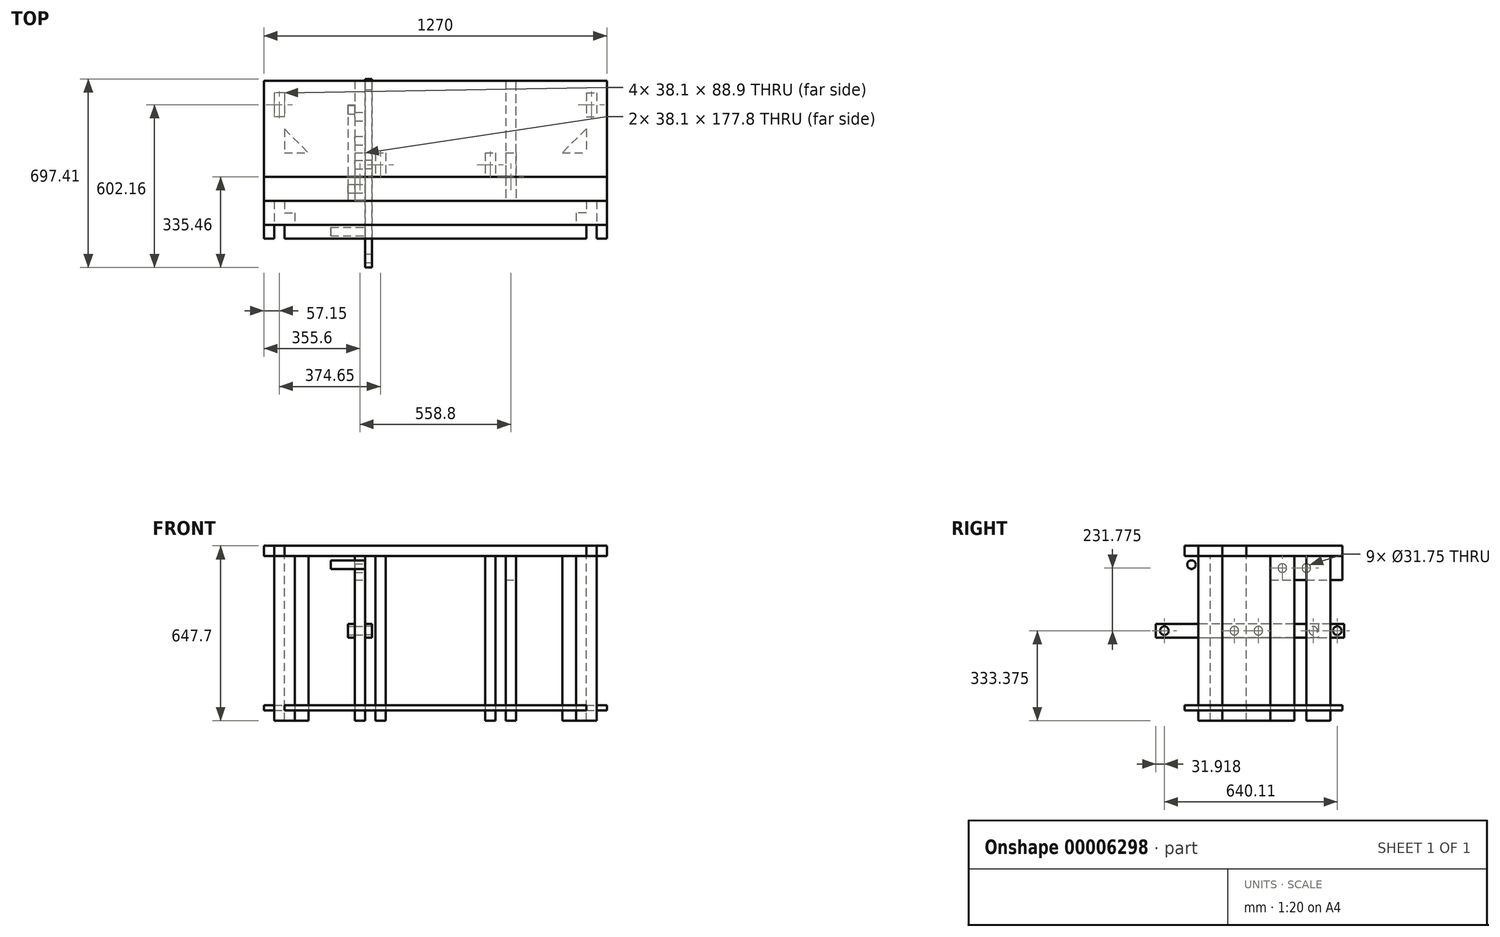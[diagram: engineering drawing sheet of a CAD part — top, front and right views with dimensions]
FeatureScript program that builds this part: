
annotation { "Feature Type Name" : "Feature", "Feature Type Description" : "" }
export const myFeature = defineFeature(function(context is Context, id is Id, definition is map)
    precondition{}
    {
        {
            var Q0;
            Q0=qCreatedBy(makeId("Top.planeOp"),FACE);
            var sketch = newSketch(context, id + "F0", { "sketchPlane" : qUnion([Q0])});
            skLineSegment(sketch, "E0.rect.bottom", {"start": v(635, -292.1) * mm, "end": v(-635, -292.1) * mm});
            skLineSegment(sketch, "E0.rect.top", {"start": v(635, 292.1) * mm, "end": v(558.8, 292.1) * mm});
            skLineSegment(sketch, "E0.rect.left", {"start": v(635, -292.1) * mm, "end": v(635, 292.1) * mm});
            skLineSegment(sketch, "E0.rect.right", {"start": v(-635, -292.1) * mm, "end": v(-635, 292.1) * mm});
            skPoint(sketch, "E0.rect.middle", {"position": v(0, 0) * mm});
            skLineSegment(sketch, "E1", {"start": v(-558.8, 292.1) * mm, "end": v(-558.8, 203.2) * mm});
            skLineSegment(sketch, "E2", {"start": v(-558.8, 203.2) * mm, "end": v(-558.8, 114.3) * mm});
            skLineSegment(sketch, "E3", {"start": v(-558.8, 114.3) * mm, "end": v(-558.8, 25.4) * mm});
            skLineSegment(sketch, "E4", {"start": v(-558.8, 203.2) * mm, "end": v(558.8, 203.2) * mm});
            skLineSegment(sketch, "E5", {"start": v(-558.8, 114.3) * mm, "end": v(558.8, 114.3) * mm});
            skLineSegment(sketch, "E6", {"start": v(-558.8, 25.4) * mm, "end": v(558.8, 25.4) * mm});
            skLineSegment(sketch, "E7", {"start": v(-558.8, 114.3) * mm, "end": v(-469.9, 25.4) * mm});
            skLineSegment(sketch, "E8", {"start": v(558.8, 114.3) * mm, "end": v(469.9, 25.4) * mm});
            skLineSegment(sketch, "E9", {"start": v(-298.45, 292.1) * mm, "end": v(-298.45, 25.4) * mm});
            skLineSegment(sketch, "E10", {"start": v(298.45, 25.4) * mm, "end": v(298.45, 292.1) * mm});
            skLineSegment(sketch, "E11", {"start": v(558.8, 292.1) * mm, "end": v(558.8, 25.4) * mm});
            skLineSegment(sketch, "E12", {"start": v(-558.8, 25.4) * mm, "end": v(-558.8, -63.5) * mm, "construction": true});
            skLineSegment(sketch, "E13", {"start": v(-558.8, -63.5) * mm, "end": v(-558.8, -152.4) * mm, "construction": true});
            skLineSegment(sketch, "E14", {"start": v(-558.8, -152.4) * mm, "end": v(-558.8, -241.3) * mm, "construction": true});
            skLineSegment(sketch, "E15", {"start": v(-558.8, -63.5) * mm, "end": v(558.8, -63.5) * mm, "construction": true});
            skLineSegment(sketch, "E16", {"start": v(-558.8, -152.4) * mm, "end": v(558.8, -152.4) * mm, "construction": true});
            skLineSegment(sketch, "E17", {"start": v(-558.8, -241.3) * mm, "end": v(558.8, -241.3) * mm, "construction": true});
            skLineSegment(sketch, "E18", {"start": v(558.8, 25.4) * mm, "end": v(558.8, -241.3) * mm, "construction": true});
            skLineSegment(sketch, "E19", {"start": v(-558.8, 292.1) * mm, "end": v(-635, 292.1) * mm});
            skLineSegment(sketch, "E20", {"start": v(-298.45, 292.1) * mm, "end": v(-558.8, 292.1) * mm});
            skLineSegment(sketch, "E21", {"start": v(298.45, 292.1) * mm, "end": v(298.45, 292.1) * mm});
            skLineSegment(sketch, "E22", {"start": v(558.8, 292.1) * mm, "end": v(298.45, 292.1) * mm});
            skLineSegment(sketch, "E23", {"start": v(-298.45, 292.1) * mm, "end": v(298.45, 292.1) * mm});
            skLineSegment(sketch, "E24", {"start": v(-260.35, 292.1) * mm, "end": v(-260.35, 25.4) * mm});
            skLineSegment(sketch, "E25", {"start": v(260.35, 292.1) * mm, "end": v(260.35, 25.4) * mm});
            skLineSegment(sketch, "E26", {"start": v(-298.45, 25.4) * mm, "end": v(-298.45, -241.3) * mm});
            skLineSegment(sketch, "E27", {"start": v(-260.35, 25.4) * mm, "end": v(-260.35, -241.3) * mm});
            skLineSegment(sketch, "E28", {"start": v(-222.25, 25.4) * mm, "end": v(-222.25, -63.5) * mm});
            skLineSegment(sketch, "E29", {"start": v(-184.15, 25.4) * mm, "end": v(-184.15, -63.5) * mm});
            skLineSegment(sketch, "E30.bottom", {"start": v(-558.8, -152.4) * mm, "end": v(-520.7, -152.4) * mm});
            skLineSegment(sketch, "E30.top", {"start": v(-558.8, -241.3) * mm, "end": v(-520.7, -241.3) * mm});
            skLineSegment(sketch, "E30.left", {"start": v(-558.8, -152.4) * mm, "end": v(-558.8, -241.3) * mm});
            skLineSegment(sketch, "E30.right", {"start": v(-520.7, -152.4) * mm, "end": v(-520.7, -241.3) * mm});
            skLineSegment(sketch, "E31.bottom", {"start": v(558.8, -152.4) * mm, "end": v(520.7, -152.4) * mm});
            skLineSegment(sketch, "E31.top", {"start": v(558.8, -241.3) * mm, "end": v(520.7, -241.3) * mm});
            skLineSegment(sketch, "E31.left", {"start": v(558.8, -152.4) * mm, "end": v(558.8, -241.3) * mm});
            skLineSegment(sketch, "E31.right", {"start": v(520.7, -152.4) * mm, "end": v(520.7, -241.3) * mm});
            skLineSegment(sketch, "E32", {"start": v(260.35, 25.4) * mm, "end": v(260.35, -241.3) * mm});
            skLineSegment(sketch, "E33", {"start": v(298.45, 25.4) * mm, "end": v(298.45, -241.3) * mm});
            skLineSegment(sketch, "E34", {"start": v(222.25, 25.4) * mm, "end": v(222.25, -63.5) * mm});
            skLineSegment(sketch, "E35", {"start": v(184.15, 25.4) * mm, "end": v(184.15, -63.5) * mm});
            skLineSegment(sketch, "E36", {"start": v(-222.25, -63.5) * mm, "end": v(-184.15, -63.5) * mm});
            skLineSegment(sketch, "E37", {"start": v(184.15, -63.5) * mm, "end": v(222.25, -63.5) * mm});
            skLineSegment(sketch, "E38", {"start": v(-298.45, -241.3) * mm, "end": v(-260.35, -241.3) * mm});
            skLineSegment(sketch, "E39", {"start": v(260.35, -241.3) * mm, "end": v(298.45, -241.3) * mm});
            skLineSegment(sketch, "E40", {"start": v(-298.45, -152.4) * mm, "end": v(-260.35, -152.4) * mm});
            skLineSegment(sketch, "E41", {"start": v(260.35, -152.4) * mm, "end": v(298.45, -152.4) * mm});
            skLineSegment(sketch, "E42", {"start": v(-558.8, 247.65) * mm, "end": v(-596.9, 247.65) * mm});
            skLineSegment(sketch, "E43", {"start": v(-596.9, 247.65) * mm, "end": v(-596.9, -292.1) * mm});
            skLineSegment(sketch, "E44", {"start": v(-596.9, -292.1) * mm, "end": v(-558.8, -292.1) * mm});
            skLineSegment(sketch, "E45", {"start": v(-558.8, -292.1) * mm, "end": v(-558.8, -241.3) * mm});
            skLineSegment(sketch, "E46", {"start": v(558.8, 247.65) * mm, "end": v(596.9, 247.65) * mm});
            skLineSegment(sketch, "E47", {"start": v(596.9, 247.65) * mm, "end": v(596.9, -292.1) * mm});
            skLineSegment(sketch, "E48", {"start": v(596.9, -292.1) * mm, "end": v(558.8, -292.1) * mm});
            skLineSegment(sketch, "E49", {"start": v(558.8, -292.1) * mm, "end": v(558.8, -241.3) * mm});
            skLineSegment(sketch, "E50", {"start": v(-558.8, 25.4) * mm, "end": v(-635, 25.4) * mm});
            skLineSegment(sketch, "E51", {"start": v(558.8, 25.4) * mm, "end": v(635, 25.4) * mm});
            skLineSegment(sketch, "E52", {"start": v(-635, -63.5) * mm, "end": v(635, -63.5) * mm});
            skLineSegment(sketch, "E53", {"start": v(-635, -152.4) * mm, "end": v(635, -152.4) * mm});
            skLineSegment(sketch, "E54", {"start": v(-635, -241.3) * mm, "end": v(635, -241.3) * mm});
            skLineSegment(sketch, "E55", {"start": v(558.8, 158.75) * mm, "end": v(596.9, 158.75) * mm});
            skLineSegment(sketch, "E56", {"start": v(-558.8, 158.75) * mm, "end": v(-596.9, 158.75) * mm});
            skLineSegment(sketch, "E57", {"start": v(-558.8, -196.85) * mm, "end": v(-520.7, -196.85) * mm});
            skLineSegment(sketch, "E58", {"start": v(558.8, -196.85) * mm, "end": v(520.7, -196.85) * mm});
            skLineSegment(sketch, "E59", {"start": v(-520.7, -241.3) * mm, "end": v(-520.7, -292.1) * mm});
            skLineSegment(sketch, "E60", {"start": v(520.7, -241.3) * mm, "end": v(520.7, -292.1) * mm});
            skSolve(sketch);
        }
        {
            var Q0;
            {var subQ3=sQuery(id+"F0.wireOp",EDGE,"E0.rect.right");var subQ5=sQuery(id+"F0.wireOp",EDGE,"E50");var subQ7=makeQuery(id+"F0.imprint","INTERSECT",VERTEX,{"derivedFrom":[subQ3,subQ5]});Q0=makeQuery(id+"F0.imprint","IMPRINT",FACE,{"disambiguationData":[TD([[makeQuery(id+"F0.imprint","IMPRINT",EDGE,{"disambiguationData":[TD([[subQ7,1.0]])],"derivedFrom":subQ3}),-1.0]])]});}
            var Q1;
            {var subQ1=sQuery(id+"F0.wireOp",EDGE,"E43");var subQ5=sQuery(id+"F0.wireOp",EDGE,"E50");var subQ6=makeQuery(id+"F0.imprint","INTERSECT",VERTEX,{"derivedFrom":[subQ1,subQ5]});Q1=makeQuery(id+"F0.imprint","IMPRINT",FACE,{"disambiguationData":[TD([[makeQuery(id+"F0.imprint","IMPRINT",EDGE,{"disambiguationData":[TD([[subQ6,-1.0]])],"derivedFrom":subQ1}),1.0]])]});}
            var Q2;
            {var subQ0=sQuery(id+"F0.wireOp",EDGE,"E52");var subQ3=sQuery(id+"F0.wireOp",EDGE,"E26");var subQ4=makeQuery(id+"F0.imprint","INTERSECT",VERTEX,{"derivedFrom":[subQ3,subQ0]});Q2=makeQuery(id+"F0.imprint","IMPRINT",FACE,{"disambiguationData":[TD([[makeQuery(id+"F0.imprint","IMPRINT",EDGE,{"disambiguationData":[TD([[subQ4,-1.0]])],"derivedFrom":subQ0}),1.0]])]});}
            var Q3;
            {var subQ3=sQuery(id+"F0.wireOp",EDGE,"E28");Q3=makeQuery(id+"F0.imprint","IMPRINT",FACE,{"disambiguationData":[TD([[makeQuery(id+"F0.imprint","IMPRINT",EDGE,{"derivedFrom":subQ3}),-1.0]])]});}
            var Q4;
            {var subQ2=sQuery(id+"F0.wireOp",EDGE,"E28");Q4=makeQuery(id+"F0.imprint","IMPRINT",FACE,{"disambiguationData":[TD([[makeQuery(id+"F0.imprint","IMPRINT",EDGE,{"derivedFrom":subQ2}),1.0]])]});}
            var Q5;
            {var subQ2=sQuery(id+"F0.wireOp",EDGE,"E29");Q5=makeQuery(id+"F0.imprint","IMPRINT",FACE,{"disambiguationData":[TD([[makeQuery(id+"F0.imprint","IMPRINT",EDGE,{"derivedFrom":subQ2}),1.0]])]});}
            var Q6;
            {var subQ2=sQuery(id+"F0.wireOp",EDGE,"E34");Q6=makeQuery(id+"F0.imprint","IMPRINT",FACE,{"disambiguationData":[TD([[makeQuery(id+"F0.imprint","IMPRINT",EDGE,{"derivedFrom":subQ2}),-1.0]])]});}
            var Q7;
            {var subQ3=sQuery(id+"F0.wireOp",EDGE,"E34");Q7=makeQuery(id+"F0.imprint","IMPRINT",FACE,{"disambiguationData":[TD([[makeQuery(id+"F0.imprint","IMPRINT",EDGE,{"derivedFrom":subQ3}),1.0]])]});}
            var Q8;
            {var subQ0=sQuery(id+"F0.wireOp",EDGE,"E52");var subQ3=sQuery(id+"F0.wireOp",EDGE,"E32");var subQ4=makeQuery(id+"F0.imprint","INTERSECT",VERTEX,{"derivedFrom":[subQ3,subQ0]});Q8=makeQuery(id+"F0.imprint","IMPRINT",FACE,{"disambiguationData":[TD([[makeQuery(id+"F0.imprint","IMPRINT",EDGE,{"disambiguationData":[TD([[subQ4,-1.0]])],"derivedFrom":subQ0}),1.0]])]});}
            var Q9;
            {var subQ1=sQuery(id+"F0.wireOp",EDGE,"E47");var subQ5=sQuery(id+"F0.wireOp",EDGE,"E51");var subQ6=makeQuery(id+"F0.imprint","INTERSECT",VERTEX,{"derivedFrom":[subQ1,subQ5]});Q9=makeQuery(id+"F0.imprint","IMPRINT",FACE,{"disambiguationData":[TD([[makeQuery(id+"F0.imprint","IMPRINT",EDGE,{"disambiguationData":[TD([[subQ6,-1.0]])],"derivedFrom":subQ1}),-1.0]])]});}
            var Q10;
            {var subQ3=sQuery(id+"F0.wireOp",EDGE,"E0.rect.left");var subQ5=sQuery(id+"F0.wireOp",EDGE,"E51");var subQ7=makeQuery(id+"F0.imprint","INTERSECT",VERTEX,{"derivedFrom":[subQ3,subQ5]});Q10=makeQuery(id+"F0.imprint","IMPRINT",FACE,{"disambiguationData":[TD([[makeQuery(id+"F0.imprint","IMPRINT",EDGE,{"disambiguationData":[TD([[subQ7,1.0]])],"derivedFrom":subQ3}),1.0]])]});}
            var Q11;
            {var subQ3=sQuery(id+"F0.wireOp",EDGE,"E0.rect.right");var subQ5=sQuery(id+"F0.wireOp",EDGE,"E53");var subQ7=makeQuery(id+"F0.imprint","INTERSECT",VERTEX,{"derivedFrom":[subQ3,subQ5]});Q11=makeQuery(id+"F0.imprint","IMPRINT",FACE,{"disambiguationData":[TD([[makeQuery(id+"F0.imprint","IMPRINT",EDGE,{"disambiguationData":[TD([[subQ7,1.0]])],"derivedFrom":subQ3}),-1.0]])]});}
            var Q12;
            {var subQ3=sQuery(id+"F0.wireOp",EDGE,"E30.left");Q12=makeQuery(id+"F0.imprint","IMPRINT",FACE,{"disambiguationData":[TD([[makeQuery(id+"F0.imprint","IMPRINT",EDGE,{"derivedFrom":subQ3}),-1.0]])]});}
            var Q13;
            {var subQ2=sQuery(id+"F0.wireOp",EDGE,"E30.left");Q13=makeQuery(id+"F0.imprint","IMPRINT",FACE,{"disambiguationData":[TD([[makeQuery(id+"F0.imprint","IMPRINT",EDGE,{"derivedFrom":subQ2}),1.0]])]});}
            var Q14;
            {var subQ1=sQuery(id+"F0.wireOp",EDGE,"E30.right");Q14=makeQuery(id+"F0.imprint","IMPRINT",FACE,{"disambiguationData":[TD([[makeQuery(id+"F0.imprint","IMPRINT",EDGE,{"derivedFrom":subQ1}),1.0]])]});}
            var Q15;
            {var subQ0=sQuery(id+"F0.wireOp",EDGE,"E54");var subQ3=sQuery(id+"F0.wireOp",EDGE,"E26");var subQ4=makeQuery(id+"F0.imprint","INTERSECT",VERTEX,{"derivedFrom":[subQ3,subQ0]});Q15=makeQuery(id+"F0.imprint","IMPRINT",FACE,{"disambiguationData":[TD([[makeQuery(id+"F0.imprint","IMPRINT",EDGE,{"disambiguationData":[TD([[subQ4,1.0]])],"derivedFrom":subQ3}),1.0]])]});}
            var Q16;
            {var subQ0=sQuery(id+"F0.wireOp",EDGE,"E54");var subQ3=sQuery(id+"F0.wireOp",EDGE,"E27");var subQ4=makeQuery(id+"F0.imprint","INTERSECT",VERTEX,{"derivedFrom":[subQ3,subQ0]});Q16=makeQuery(id+"F0.imprint","IMPRINT",FACE,{"disambiguationData":[TD([[makeQuery(id+"F0.imprint","IMPRINT",EDGE,{"disambiguationData":[TD([[subQ4,1.0]])],"derivedFrom":subQ3}),1.0]])]});}
            var Q17;
            {var subQ0=sQuery(id+"F0.wireOp",EDGE,"E54");var subQ3=sQuery(id+"F0.wireOp",EDGE,"E32");var subQ4=makeQuery(id+"F0.imprint","INTERSECT",VERTEX,{"derivedFrom":[subQ3,subQ0]});Q17=makeQuery(id+"F0.imprint","IMPRINT",FACE,{"disambiguationData":[TD([[makeQuery(id+"F0.imprint","IMPRINT",EDGE,{"disambiguationData":[TD([[subQ4,1.0]])],"derivedFrom":subQ3}),1.0]])]});}
            var Q18;
            {var subQ3=sQuery(id+"F0.wireOp",EDGE,"E31.right");Q18=makeQuery(id+"F0.imprint","IMPRINT",FACE,{"disambiguationData":[TD([[makeQuery(id+"F0.imprint","IMPRINT",EDGE,{"derivedFrom":subQ3}),-1.0]])]});}
            var Q19;
            {var subQ2=sQuery(id+"F0.wireOp",EDGE,"E31.left");Q19=makeQuery(id+"F0.imprint","IMPRINT",FACE,{"disambiguationData":[TD([[makeQuery(id+"F0.imprint","IMPRINT",EDGE,{"derivedFrom":subQ2}),-1.0]])]});}
            var Q20;
            {var subQ3=sQuery(id+"F0.wireOp",EDGE,"E31.left");Q20=makeQuery(id+"F0.imprint","IMPRINT",FACE,{"disambiguationData":[TD([[makeQuery(id+"F0.imprint","IMPRINT",EDGE,{"derivedFrom":subQ3}),1.0]])]});}
            var Q21;
            {var subQ3=sQuery(id+"F0.wireOp",EDGE,"E0.rect.left");var subQ5=sQuery(id+"F0.wireOp",EDGE,"E53");var subQ7=makeQuery(id+"F0.imprint","INTERSECT",VERTEX,{"derivedFrom":[subQ3,subQ5]});Q21=makeQuery(id+"F0.imprint","IMPRINT",FACE,{"disambiguationData":[TD([[makeQuery(id+"F0.imprint","IMPRINT",EDGE,{"disambiguationData":[TD([[subQ7,1.0]])],"derivedFrom":subQ3}),1.0]])]});}
            extrude(context, id + "F1", {"entities" : qUnion([Q0, Q1, Q2, Q3, Q4, Q5, Q6, Q7, Q8, Q9, Q10, Q11, Q12, Q13, Q14, Q15, Q16, Q17, Q18, Q19, Q20, Q21]), "depth" : 38.1 * mm});
        }
        {
            var Q0;
            {var subQ3=sQuery(id+"F0.wireOp",EDGE,"E0.rect.right");var subQ5=sQuery(id+"F0.wireOp",EDGE,"E52");var subQ7=makeQuery(id+"F0.imprint","INTERSECT",VERTEX,{"derivedFrom":[subQ3,subQ5]});Q0=makeQuery(id+"F0.imprint","IMPRINT",FACE,{"disambiguationData":[TD([[makeQuery(id+"F0.imprint","IMPRINT",EDGE,{"disambiguationData":[TD([[subQ7,1.0]])],"derivedFrom":subQ3}),-1.0]])]});}
            var Q1;
            {var subQ3=sQuery(id+"F0.wireOp",EDGE,"E26");var subQ5=sQuery(id+"F0.wireOp",EDGE,"E52");var subQ7=makeQuery(id+"F0.imprint","INTERSECT",VERTEX,{"derivedFrom":[subQ3,subQ5]});Q1=makeQuery(id+"F0.imprint","IMPRINT",FACE,{"disambiguationData":[TD([[makeQuery(id+"F0.imprint","IMPRINT",EDGE,{"disambiguationData":[TD([[subQ7,-1.0]])],"derivedFrom":subQ3}),1.0]])]});}
            var Q2;
            {var subQ1=sQuery(id+"F0.wireOp",EDGE,"E26");var subQ7=sQuery(id+"F0.wireOp",EDGE,"E52");var subQ9=makeQuery(id+"F0.imprint","INTERSECT",VERTEX,{"derivedFrom":[subQ1,subQ7]});Q2=makeQuery(id+"F0.imprint","IMPRINT",FACE,{"disambiguationData":[TD([[makeQuery(id+"F0.imprint","IMPRINT",EDGE,{"disambiguationData":[TD([[subQ9,-1.0]])],"derivedFrom":subQ1}),-1.0]])]});}
            var Q3;
            {var subQ3=sQuery(id+"F0.wireOp",EDGE,"E27");var subQ5=sQuery(id+"F0.wireOp",EDGE,"E52");var subQ11=makeQuery(id+"F0.imprint","INTERSECT",VERTEX,{"derivedFrom":[subQ3,subQ5]});Q3=makeQuery(id+"F0.imprint","IMPRINT",FACE,{"disambiguationData":[TD([[makeQuery(id+"F0.imprint","IMPRINT",EDGE,{"disambiguationData":[TD([[subQ11,-1.0]])],"derivedFrom":subQ3}),1.0]])]});}
            var Q4;
            {var subQ3=sQuery(id+"F0.wireOp",EDGE,"E32");var subQ5=sQuery(id+"F0.wireOp",EDGE,"E52");var subQ7=makeQuery(id+"F0.imprint","INTERSECT",VERTEX,{"derivedFrom":[subQ3,subQ5]});Q4=makeQuery(id+"F0.imprint","IMPRINT",FACE,{"disambiguationData":[TD([[makeQuery(id+"F0.imprint","IMPRINT",EDGE,{"disambiguationData":[TD([[subQ7,-1.0]])],"derivedFrom":subQ3}),1.0]])]});}
            var Q5;
            {var subQ5=sQuery(id+"F0.wireOp",EDGE,"E33");var subQ7=sQuery(id+"F0.wireOp",EDGE,"E52");var subQ9=makeQuery(id+"F0.imprint","INTERSECT",VERTEX,{"derivedFrom":[subQ5,subQ7]});Q5=makeQuery(id+"F0.imprint","IMPRINT",FACE,{"disambiguationData":[TD([[makeQuery(id+"F0.imprint","IMPRINT",EDGE,{"disambiguationData":[TD([[subQ9,-1.0]])],"derivedFrom":subQ5}),1.0]])]});}
            var Q6;
            {var subQ3=sQuery(id+"F0.wireOp",EDGE,"E0.rect.left");var subQ5=sQuery(id+"F0.wireOp",EDGE,"E52");var subQ7=makeQuery(id+"F0.imprint","INTERSECT",VERTEX,{"derivedFrom":[subQ3,subQ5]});Q6=makeQuery(id+"F0.imprint","IMPRINT",FACE,{"disambiguationData":[TD([[makeQuery(id+"F0.imprint","IMPRINT",EDGE,{"disambiguationData":[TD([[subQ7,1.0]])],"derivedFrom":subQ3}),1.0]])]});}
            var Q7;
            {var subQ3=sQuery(id+"F0.wireOp",EDGE,"E0.rect.left");var subQ5=sQuery(id+"F0.wireOp",EDGE,"E0.rect.bottom");var subQ7=makeQuery(id+"F0.imprint","INTERSECT",VERTEX,{"derivedFrom":[subQ5,subQ3]});Q7=makeQuery(id+"F0.imprint","IMPRINT",FACE,{"disambiguationData":[TD([[makeQuery(id+"F0.imprint","IMPRINT",EDGE,{"disambiguationData":[TD([[subQ7,-1.0]])],"derivedFrom":subQ3}),1.0]])]});}
            var Q8;
            {var subQ4=sQuery(id+"F0.wireOp",EDGE,"E48");Q8=makeQuery(id+"F0.imprint","IMPRINT",FACE,{"disambiguationData":[TD([[makeQuery(id+"F0.imprint","IMPRINT",EDGE,{"derivedFrom":subQ4}),-1.0]])]});}
            var Q9;
            {var subQ8=sQuery(id+"F0.wireOp",EDGE,"E45");Q9=makeQuery(id+"F0.imprint","IMPRINT",FACE,{"disambiguationData":[TD([[makeQuery(id+"F0.imprint","IMPRINT",EDGE,{"derivedFrom":subQ8}),-1.0]])]});}
            var Q10;
            {var subQ4=sQuery(id+"F0.wireOp",EDGE,"E44");Q10=makeQuery(id+"F0.imprint","IMPRINT",FACE,{"disambiguationData":[TD([[makeQuery(id+"F0.imprint","IMPRINT",EDGE,{"derivedFrom":subQ4}),1.0]])]});}
            var Q11;
            {var subQ3=sQuery(id+"F0.wireOp",EDGE,"E0.rect.bottom");var subQ5=sQuery(id+"F0.wireOp",EDGE,"E0.rect.right");var subQ7=makeQuery(id+"F0.imprint","INTERSECT",VERTEX,{"derivedFrom":[subQ3,subQ5]});Q11=makeQuery(id+"F0.imprint","IMPRINT",FACE,{"disambiguationData":[TD([[makeQuery(id+"F0.imprint","IMPRINT",EDGE,{"disambiguationData":[TD([[subQ7,-1.0]])],"derivedFrom":subQ5}),-1.0]])]});}
            var Q12;
            {var subQ2=sQuery(id+"F0.wireOp",EDGE,"E3");Q12=makeQuery(id+"F0.imprint","IMPRINT",FACE,{"disambiguationData":[TD([[makeQuery(id+"F0.imprint","IMPRINT",EDGE,{"derivedFrom":subQ2}),1.0]])]});}
            var Q13;
            {var subQ5=sQuery(id+"F0.wireOp",EDGE,"E2");Q13=makeQuery(id+"F0.imprint","IMPRINT",FACE,{"disambiguationData":[TD([[makeQuery(id+"F0.imprint","IMPRINT",EDGE,{"derivedFrom":subQ5}),-1.0]])]});}
            var Q14;
            {var subQ6=sQuery(id+"F0.wireOp",EDGE,"E19");Q14=makeQuery(id+"F0.imprint","IMPRINT",FACE,{"disambiguationData":[TD([[makeQuery(id+"F0.imprint","IMPRINT",EDGE,{"derivedFrom":subQ6}),1.0]])]});}
            var Q15;
            {var subQ3=sQuery(id+"F0.wireOp",EDGE,"E8");Q15=makeQuery(id+"F0.imprint","IMPRINT",FACE,{"disambiguationData":[TD([[makeQuery(id+"F0.imprint","IMPRINT",EDGE,{"derivedFrom":subQ3}),1.0]])]});}
            var Q16;
            {var subQ5=sQuery(id+"F0.wireOp",EDGE,"E46");Q16=makeQuery(id+"F0.imprint","IMPRINT",FACE,{"disambiguationData":[TD([[makeQuery(id+"F0.imprint","IMPRINT",EDGE,{"derivedFrom":subQ5}),-1.0]])]});}
            var Q17;
            {var subQ7=sQuery(id+"F0.wireOp",EDGE,"E0.rect.top");Q17=makeQuery(id+"F0.imprint","IMPRINT",FACE,{"disambiguationData":[TD([[makeQuery(id+"F0.imprint","IMPRINT",EDGE,{"derivedFrom":subQ7}),1.0]])]});}
            var Q18;
            {var subQ5=sQuery(id+"F0.wireOp",EDGE,"E55");Q18=makeQuery(id+"F0.imprint","IMPRINT",FACE,{"disambiguationData":[TD([[makeQuery(id+"F0.imprint","IMPRINT",EDGE,{"derivedFrom":subQ5}),-1.0]])]});}
            var Q19;
            {var subQ1=sQuery(id+"F0.wireOp",EDGE,"E59");Q19=makeQuery(id+"F0.imprint","IMPRINT",FACE,{"disambiguationData":[TD([[makeQuery(id+"F0.imprint","IMPRINT",EDGE,{"derivedFrom":subQ1}),1.0]])]});}
            var Q20;
            {var subQ2=sQuery(id+"F0.wireOp",EDGE,"E49");Q20=makeQuery(id+"F0.imprint","IMPRINT",FACE,{"disambiguationData":[TD([[makeQuery(id+"F0.imprint","IMPRINT",EDGE,{"derivedFrom":subQ2}),1.0]])]});}
            extrude(context, id + "F2", {"entities" : qUnion([Q0, Q1, Q2, Q3, Q4, Q5, Q6, Q7, Q8, Q9, Q10, Q11, Q12, Q13, Q14, Q15, Q16, Q17, Q18, Q19, Q20]), "depth" : 38.1 * mm});
        }
        {
            var Q0;
            {var subQ0=sQuery(id+"F0.wireOp",EDGE,"E0.rect.right");Q0=makeQuery(id+"F1.opExtrude","SWEPT_FACE",FACE,{"disambiguationData":[OSD([subQ0]),TDD([makeQuery(id+"F0.imprint","IMPRINT",EDGE,{"disambiguationData":[TD([[makeQuery(id+"F0.imprint","INTERSECT",VERTEX,{"derivedFrom":[subQ0,sQuery(id+"F0.wireOp",EDGE,"E50")]}),1.0]])],"derivedFrom":subQ0})])]});}
            var sketch = newSketch(context, id + "F3", { "sketchPlane" : qUnion([Q0])});
            skPoint(sketch, "E61", {"position": v(-292.1, 0) * mm});
            skPoint(sketch, "E62", {"position": v(292.1, 0) * mm});
            skLineSegment(sketch, "E63", {"start": v(-292.1, 0) * mm, "end": v(292.1, 0) * mm});
            skLineSegment(sketch, "E64", {"start": v(292.1, 0) * mm, "end": v(292.1, 38.1) * mm});
            skLineSegment(sketch, "E65", {"start": v(292.1, 38.1) * mm, "end": v(-292.1, 38.1) * mm});
            skLineSegment(sketch, "E66", {"start": v(-292.1, 38.1) * mm, "end": v(-292.1, 0) * mm});
            skLineSegment(sketch, "E67", {"start": v(241.3, 0) * mm, "end": v(241.3, -609.6) * mm});
            skLineSegment(sketch, "E68", {"start": v(241.3, -609.6) * mm, "end": v(152.4, -609.6) * mm});
            skLineSegment(sketch, "E69", {"start": v(152.4, -609.6) * mm, "end": v(152.4, 0) * mm});
            skLineSegment(sketch, "E70", {"start": v(-114.3, 0) * mm, "end": v(-114.3, -609.6) * mm});
            skLineSegment(sketch, "E71", {"start": v(-25.4, 0) * mm, "end": v(-25.4, -609.6) * mm});
            skLineSegment(sketch, "E72", {"start": v(-114.3, -609.6) * mm, "end": v(-25.4, -609.6) * mm});
            skLineSegment(sketch, "E73", {"start": v(292.1, -571.5) * mm, "end": v(-292.1, -571.5) * mm});
            skLineSegment(sketch, "E74", {"start": v(-292.1, -571.5) * mm, "end": v(-292.1, -552.45) * mm});
            skLineSegment(sketch, "E75", {"start": v(-292.1, -552.45) * mm, "end": v(292.1, -552.45) * mm});
            skLineSegment(sketch, "E76", {"start": v(292.1, -552.45) * mm, "end": v(292.1, -571.5) * mm});
            skLineSegment(sketch, "E77", {"start": v(-247.65, 0) * mm, "end": v(-247.65, -609.6) * mm});
            skLineSegment(sketch, "E78", {"start": v(-247.65, -609.6) * mm, "end": v(-158.75, -609.6) * mm});
            skLineSegment(sketch, "E79", {"start": v(-158.75, -609.6) * mm, "end": v(-158.75, 0) * mm});
            skLineSegment(sketch, "E80", {"start": v(-158.75, -88.9) * mm, "end": v(152.4, -88.9) * mm});
            skLineSegment(sketch, "E81", {"start": v(241.3, -88.9) * mm, "end": v(279.4, -88.9) * mm});
            skLineSegment(sketch, "E82", {"start": v(279.4, -88.9) * mm, "end": v(279.4, 0) * mm});
            skSolve(sketch);
        }
        {
            var Q0;
            {var subQ2=sQuery(id+"F0.wireOp",EDGE,"E42");Q0=makeQuery(id+"F0.imprint","IMPRINT",FACE,{"disambiguationData":[TD([[makeQuery(id+"F0.imprint","IMPRINT",EDGE,{"derivedFrom":subQ2}),1.0]])]});}
            var Q1;
            {var subQ2=sQuery(id+"F0.wireOp",EDGE,"E46");Q1=makeQuery(id+"F0.imprint","IMPRINT",FACE,{"disambiguationData":[TD([[makeQuery(id+"F0.imprint","IMPRINT",EDGE,{"derivedFrom":subQ2}),-1.0]])]});}
            var Q2;
            {var subQ3=sQuery(id+"F0.wireOp",EDGE,"E8");Q2=makeQuery(id+"F0.imprint","IMPRINT",FACE,{"disambiguationData":[TD([[makeQuery(id+"F0.imprint","IMPRINT",EDGE,{"derivedFrom":subQ3}),1.0]])]});}
            var Q3;
            {var subQ2=sQuery(id+"F0.wireOp",EDGE,"E3");Q3=makeQuery(id+"F0.imprint","IMPRINT",FACE,{"disambiguationData":[TD([[makeQuery(id+"F0.imprint","IMPRINT",EDGE,{"derivedFrom":subQ2}),1.0]])]});}
            var Q4;
            {var subQ0=sQuery(id+"F0.wireOp",EDGE,"E52");var subQ3=sQuery(id+"F0.wireOp",EDGE,"E26");var subQ4=makeQuery(id+"F0.imprint","INTERSECT",VERTEX,{"derivedFrom":[subQ3,subQ0]});Q4=makeQuery(id+"F0.imprint","IMPRINT",FACE,{"disambiguationData":[TD([[makeQuery(id+"F0.imprint","IMPRINT",EDGE,{"disambiguationData":[TD([[subQ4,-1.0]])],"derivedFrom":subQ0}),1.0]])]});}
            var Q5;
            {var subQ3=sQuery(id+"F0.wireOp",EDGE,"E26");var subQ5=sQuery(id+"F0.wireOp",EDGE,"E52");var subQ7=makeQuery(id+"F0.imprint","INTERSECT",VERTEX,{"derivedFrom":[subQ3,subQ5]});Q5=makeQuery(id+"F0.imprint","IMPRINT",FACE,{"disambiguationData":[TD([[makeQuery(id+"F0.imprint","IMPRINT",EDGE,{"disambiguationData":[TD([[subQ7,-1.0]])],"derivedFrom":subQ3}),1.0]])]});}
            var Q6;
            {var subQ2=sQuery(id+"F0.wireOp",EDGE,"E28");Q6=makeQuery(id+"F0.imprint","IMPRINT",FACE,{"disambiguationData":[TD([[makeQuery(id+"F0.imprint","IMPRINT",EDGE,{"derivedFrom":subQ2}),1.0]])]});}
            var Q7;
            {var subQ2=sQuery(id+"F0.wireOp",EDGE,"E34");Q7=makeQuery(id+"F0.imprint","IMPRINT",FACE,{"disambiguationData":[TD([[makeQuery(id+"F0.imprint","IMPRINT",EDGE,{"derivedFrom":subQ2}),-1.0]])]});}
            var Q8;
            {var subQ0=sQuery(id+"F0.wireOp",EDGE,"E52");var subQ3=sQuery(id+"F0.wireOp",EDGE,"E32");var subQ4=makeQuery(id+"F0.imprint","INTERSECT",VERTEX,{"derivedFrom":[subQ3,subQ0]});Q8=makeQuery(id+"F0.imprint","IMPRINT",FACE,{"disambiguationData":[TD([[makeQuery(id+"F0.imprint","IMPRINT",EDGE,{"disambiguationData":[TD([[subQ4,-1.0]])],"derivedFrom":subQ0}),1.0]])]});}
            var Q9;
            {var subQ0=sQuery(id+"F0.wireOp",EDGE,"E52");var subQ3=sQuery(id+"F0.wireOp",EDGE,"E32");var subQ4=makeQuery(id+"F0.imprint","INTERSECT",VERTEX,{"derivedFrom":[subQ3,subQ0]});Q9=makeQuery(id+"F0.imprint","IMPRINT",FACE,{"disambiguationData":[TD([[makeQuery(id+"F0.imprint","IMPRINT",EDGE,{"disambiguationData":[TD([[subQ4,-1.0]])],"derivedFrom":subQ3}),1.0]])]});}
            var Q10;
            {var subQ3=sQuery(id+"F0.wireOp",EDGE,"E30.left");var subQ5=sQuery(id+"F0.wireOp",EDGE,"E53");var subQ7=makeQuery(id+"F0.imprint","INTERSECT",VERTEX,{"derivedFrom":[subQ3,subQ5]});Q10=makeQuery(id+"F0.imprint","IMPRINT",FACE,{"disambiguationData":[TD([[makeQuery(id+"F0.imprint","IMPRINT",EDGE,{"disambiguationData":[TD([[subQ7,-1.0]])],"derivedFrom":subQ3}),-1.0]])]});}
            var Q11;
            {var subQ0=sQuery(id+"F0.wireOp",EDGE,"E57");Q11=makeQuery(id+"F0.imprint","IMPRINT",FACE,{"disambiguationData":[TD([[makeQuery(id+"F0.imprint","IMPRINT",EDGE,{"derivedFrom":subQ0}),-1.0]])]});}
            var Q12;
            {var subQ0=sQuery(id+"F0.wireOp",EDGE,"E58");Q12=makeQuery(id+"F0.imprint","IMPRINT",FACE,{"disambiguationData":[TD([[makeQuery(id+"F0.imprint","IMPRINT",EDGE,{"derivedFrom":subQ0}),1.0]])]});}
            var Q13;
            {var subQ3=sQuery(id+"F0.wireOp",EDGE,"E31.left");var subQ5=sQuery(id+"F0.wireOp",EDGE,"E53");var subQ7=makeQuery(id+"F0.imprint","INTERSECT",VERTEX,{"derivedFrom":[subQ3,subQ5]});Q13=makeQuery(id+"F0.imprint","IMPRINT",FACE,{"disambiguationData":[TD([[makeQuery(id+"F0.imprint","IMPRINT",EDGE,{"disambiguationData":[TD([[subQ7,-1.0]])],"derivedFrom":subQ3}),1.0]])]});}
            extrude(context, id + "F4", {"entities" : qUnion([Q0, Q1, Q2, Q3, Q4, Q5, Q6, Q7, Q8, Q9, Q10, Q11, Q12, Q13]), "oppositeDirection" : true, "depth" : 609.6 * mm});
        }
        {
            var Q0;
            {var subQ7=sQuery(id+"F0.wireOp",EDGE,"E19");Q0=makeQuery(id+"F0.imprint","IMPRINT",FACE,{"disambiguationData":[TD([[makeQuery(id+"F0.imprint","IMPRINT",EDGE,{"derivedFrom":subQ7}),1.0]])]});}
            var Q1;
            {var subQ0=sQuery(id+"F0.wireOp",EDGE,"E20");Q1=makeQuery(id+"F0.imprint","IMPRINT",FACE,{"disambiguationData":[TD([[makeQuery(id+"F0.imprint","IMPRINT",EDGE,{"derivedFrom":subQ0}),1.0]])]});}
            var Q2;
            {var subQ1=sQuery(id+"F0.wireOp",EDGE,"E4");var subQ5=sQuery(id+"F0.wireOp",EDGE,"E9");var subQ7=makeQuery(id+"F0.imprint","INTERSECT",VERTEX,{"derivedFrom":[subQ1,subQ5]});Q2=makeQuery(id+"F0.imprint","IMPRINT",FACE,{"disambiguationData":[TD([[makeQuery(id+"F0.imprint","IMPRINT",EDGE,{"disambiguationData":[TD([[subQ7,-1.0]])],"derivedFrom":subQ1}),1.0]])]});}
            var Q3;
            {var subQ1=sQuery(id+"F0.wireOp",EDGE,"E4");var subQ5=sQuery(id+"F0.wireOp",EDGE,"E24");var subQ6=makeQuery(id+"F0.imprint","INTERSECT",VERTEX,{"derivedFrom":[subQ1,subQ5]});Q3=makeQuery(id+"F0.imprint","IMPRINT",FACE,{"disambiguationData":[TD([[makeQuery(id+"F0.imprint","IMPRINT",EDGE,{"disambiguationData":[TD([[subQ6,-1.0]])],"derivedFrom":subQ1}),1.0]])]});}
            var Q4;
            {var subQ0=sQuery(id+"F0.wireOp",EDGE,"E25");var subQ1=sQuery(id+"F0.wireOp",EDGE,"E4");var subQ2=makeQuery(id+"F0.imprint","INTERSECT",VERTEX,{"derivedFrom":[subQ1,subQ0]});Q4=makeQuery(id+"F0.imprint","IMPRINT",FACE,{"disambiguationData":[TD([[makeQuery(id+"F0.imprint","IMPRINT",EDGE,{"disambiguationData":[TD([[subQ2,-1.0]])],"derivedFrom":subQ1}),1.0]])]});}
            var Q5;
            {var subQ0=sQuery(id+"F0.wireOp",EDGE,"E22");Q5=makeQuery(id+"F0.imprint","IMPRINT",FACE,{"disambiguationData":[TD([[makeQuery(id+"F0.imprint","IMPRINT",EDGE,{"derivedFrom":subQ0}),1.0]])]});}
            var Q6;
            {var subQ8=sQuery(id+"F0.wireOp",EDGE,"E0.rect.top");Q6=makeQuery(id+"F0.imprint","IMPRINT",FACE,{"disambiguationData":[TD([[makeQuery(id+"F0.imprint","IMPRINT",EDGE,{"derivedFrom":subQ8}),1.0]])]});}
            var Q7;
            {var subQ0=sQuery(id+"F0.wireOp",EDGE,"E55");Q7=makeQuery(id+"F0.imprint","IMPRINT",FACE,{"disambiguationData":[TD([[makeQuery(id+"F0.imprint","IMPRINT",EDGE,{"derivedFrom":subQ0}),-1.0]])]});}
            var Q8;
            {var subQ5=sQuery(id+"F0.wireOp",EDGE,"E8");Q8=makeQuery(id+"F0.imprint","IMPRINT",FACE,{"disambiguationData":[TD([[makeQuery(id+"F0.imprint","IMPRINT",EDGE,{"derivedFrom":subQ5}),-1.0]])]});}
            var Q9;
            {var subQ0=sQuery(id+"F0.wireOp",EDGE,"E11");var subQ4=sQuery(id+"F0.wireOp",EDGE,"E4");var subQ5=makeQuery(id+"F0.imprint","INTERSECT",VERTEX,{"derivedFrom":[subQ4,subQ0]});Q9=makeQuery(id+"F0.imprint","IMPRINT",FACE,{"disambiguationData":[TD([[makeQuery(id+"F0.imprint","IMPRINT",EDGE,{"disambiguationData":[TD([[subQ5,1.0]])],"derivedFrom":subQ4}),-1.0]])]});}
            var Q10;
            {var subQ0=sQuery(id+"F0.wireOp",EDGE,"E25");var subQ3=sQuery(id+"F0.wireOp",EDGE,"E4");var subQ4=makeQuery(id+"F0.imprint","INTERSECT",VERTEX,{"derivedFrom":[subQ3,subQ0]});Q10=makeQuery(id+"F0.imprint","IMPRINT",FACE,{"disambiguationData":[TD([[makeQuery(id+"F0.imprint","IMPRINT",EDGE,{"disambiguationData":[TD([[subQ4,-1.0]])],"derivedFrom":subQ3}),-1.0]])]});}
            var Q11;
            {var subQ3=sQuery(id+"F0.wireOp",EDGE,"E4");var subQ5=sQuery(id+"F0.wireOp",EDGE,"E24");var subQ7=makeQuery(id+"F0.imprint","INTERSECT",VERTEX,{"derivedFrom":[subQ3,subQ5]});Q11=makeQuery(id+"F0.imprint","IMPRINT",FACE,{"disambiguationData":[TD([[makeQuery(id+"F0.imprint","IMPRINT",EDGE,{"disambiguationData":[TD([[subQ7,-1.0]])],"derivedFrom":subQ3}),-1.0]])]});}
            var Q12;
            {var subQ3=sQuery(id+"F0.wireOp",EDGE,"E4");var subQ5=sQuery(id+"F0.wireOp",EDGE,"E9");var subQ7=makeQuery(id+"F0.imprint","INTERSECT",VERTEX,{"derivedFrom":[subQ3,subQ5]});Q12=makeQuery(id+"F0.imprint","IMPRINT",FACE,{"disambiguationData":[TD([[makeQuery(id+"F0.imprint","IMPRINT",EDGE,{"disambiguationData":[TD([[subQ7,-1.0]])],"derivedFrom":subQ3}),-1.0]])]});}
            var Q13;
            {var subQ0=sQuery(id+"F0.wireOp",EDGE,"E9");var subQ3=sQuery(id+"F0.wireOp",EDGE,"E4");var subQ4=makeQuery(id+"F0.imprint","INTERSECT",VERTEX,{"derivedFrom":[subQ3,subQ0]});Q13=makeQuery(id+"F0.imprint","IMPRINT",FACE,{"disambiguationData":[TD([[makeQuery(id+"F0.imprint","IMPRINT",EDGE,{"disambiguationData":[TD([[subQ4,-1.0]])],"derivedFrom":subQ0}),-1.0]])]});}
            var Q14;
            {var subQ4=sQuery(id+"F0.wireOp",EDGE,"E3");Q14=makeQuery(id+"F0.imprint","IMPRINT",FACE,{"disambiguationData":[TD([[makeQuery(id+"F0.imprint","IMPRINT",EDGE,{"derivedFrom":subQ4}),-1.0]])]});}
            var Q15;
            {var subQ5=sQuery(id+"F0.wireOp",EDGE,"E7");Q15=makeQuery(id+"F0.imprint","IMPRINT",FACE,{"disambiguationData":[TD([[makeQuery(id+"F0.imprint","IMPRINT",EDGE,{"derivedFrom":subQ5}),1.0]])]});}
            var Q16;
            {var subQ1=sQuery(id+"F0.wireOp",EDGE,"E43");var subQ5=sQuery(id+"F0.wireOp",EDGE,"E50");var subQ6=makeQuery(id+"F0.imprint","INTERSECT",VERTEX,{"derivedFrom":[subQ1,subQ5]});Q16=makeQuery(id+"F0.imprint","IMPRINT",FACE,{"disambiguationData":[TD([[makeQuery(id+"F0.imprint","IMPRINT",EDGE,{"disambiguationData":[TD([[subQ6,-1.0]])],"derivedFrom":subQ1}),1.0]])]});}
            var Q17;
            {var subQ3=sQuery(id+"F0.wireOp",EDGE,"E0.rect.right");var subQ5=sQuery(id+"F0.wireOp",EDGE,"E50");var subQ7=makeQuery(id+"F0.imprint","INTERSECT",VERTEX,{"derivedFrom":[subQ3,subQ5]});Q17=makeQuery(id+"F0.imprint","IMPRINT",FACE,{"disambiguationData":[TD([[makeQuery(id+"F0.imprint","IMPRINT",EDGE,{"disambiguationData":[TD([[subQ7,1.0]])],"derivedFrom":subQ3}),-1.0]])]});}
            var Q18;
            {var subQ3=sQuery(id+"F0.wireOp",EDGE,"E0.rect.right");var subQ5=sQuery(id+"F0.wireOp",EDGE,"E52");var subQ7=makeQuery(id+"F0.imprint","INTERSECT",VERTEX,{"derivedFrom":[subQ3,subQ5]});Q18=makeQuery(id+"F0.imprint","IMPRINT",FACE,{"disambiguationData":[TD([[makeQuery(id+"F0.imprint","IMPRINT",EDGE,{"disambiguationData":[TD([[subQ7,1.0]])],"derivedFrom":subQ3}),-1.0]])]});}
            var Q19;
            {var subQ1=sQuery(id+"F0.wireOp",EDGE,"E26");var subQ7=sQuery(id+"F0.wireOp",EDGE,"E52");var subQ9=makeQuery(id+"F0.imprint","INTERSECT",VERTEX,{"derivedFrom":[subQ1,subQ7]});Q19=makeQuery(id+"F0.imprint","IMPRINT",FACE,{"disambiguationData":[TD([[makeQuery(id+"F0.imprint","IMPRINT",EDGE,{"disambiguationData":[TD([[subQ9,-1.0]])],"derivedFrom":subQ1}),-1.0]])]});}
            var Q20;
            {var subQ3=sQuery(id+"F0.wireOp",EDGE,"E0.rect.right");var subQ5=sQuery(id+"F0.wireOp",EDGE,"E53");var subQ7=makeQuery(id+"F0.imprint","INTERSECT",VERTEX,{"derivedFrom":[subQ3,subQ5]});Q20=makeQuery(id+"F0.imprint","IMPRINT",FACE,{"disambiguationData":[TD([[makeQuery(id+"F0.imprint","IMPRINT",EDGE,{"disambiguationData":[TD([[subQ7,1.0]])],"derivedFrom":subQ3}),-1.0]])]});}
            var Q21;
            {var subQ3=sQuery(id+"F0.wireOp",EDGE,"E0.rect.right");var subQ5=sQuery(id+"F0.wireOp",EDGE,"E0.rect.bottom");var subQ7=makeQuery(id+"F0.imprint","INTERSECT",VERTEX,{"derivedFrom":[subQ5,subQ3]});Q21=makeQuery(id+"F0.imprint","IMPRINT",FACE,{"disambiguationData":[TD([[makeQuery(id+"F0.imprint","IMPRINT",EDGE,{"disambiguationData":[TD([[subQ7,-1.0]])],"derivedFrom":subQ3}),-1.0]])]});}
            var Q22;
            {var subQ4=sQuery(id+"F0.wireOp",EDGE,"E44");Q22=makeQuery(id+"F0.imprint","IMPRINT",FACE,{"disambiguationData":[TD([[makeQuery(id+"F0.imprint","IMPRINT",EDGE,{"derivedFrom":subQ4}),1.0]])]});}
            var Q23;
            {var subQ2=sQuery(id+"F0.wireOp",EDGE,"E45");Q23=makeQuery(id+"F0.imprint","IMPRINT",FACE,{"disambiguationData":[TD([[makeQuery(id+"F0.imprint","IMPRINT",EDGE,{"derivedFrom":subQ2}),-1.0]])]});}
            var Q24;
            {var subQ0=sQuery(id+"F0.wireOp",EDGE,"E57");Q24=makeQuery(id+"F0.imprint","IMPRINT",FACE,{"disambiguationData":[TD([[makeQuery(id+"F0.imprint","IMPRINT",EDGE,{"derivedFrom":subQ0}),1.0]])]});}
            var Q25;
            {var subQ0=sQuery(id+"F0.wireOp",EDGE,"E54");var subQ3=sQuery(id+"F0.wireOp",EDGE,"E26");var subQ4=makeQuery(id+"F0.imprint","INTERSECT",VERTEX,{"derivedFrom":[subQ3,subQ0]});Q25=makeQuery(id+"F0.imprint","IMPRINT",FACE,{"disambiguationData":[TD([[makeQuery(id+"F0.imprint","IMPRINT",EDGE,{"disambiguationData":[TD([[subQ4,1.0]])],"derivedFrom":subQ3}),-1.0]])]});}
            var Q26;
            {var subQ0=sQuery(id+"F0.wireOp",EDGE,"E54");var subQ3=sQuery(id+"F0.wireOp",EDGE,"E26");var subQ4=makeQuery(id+"F0.imprint","INTERSECT",VERTEX,{"derivedFrom":[subQ3,subQ0]});Q26=makeQuery(id+"F0.imprint","IMPRINT",FACE,{"disambiguationData":[TD([[makeQuery(id+"F0.imprint","IMPRINT",EDGE,{"disambiguationData":[TD([[subQ4,1.0]])],"derivedFrom":subQ3}),1.0]])]});}
            var Q27;
            {var subQ0=sQuery(id+"F0.wireOp",EDGE,"E54");var subQ3=sQuery(id+"F0.wireOp",EDGE,"E27");var subQ4=makeQuery(id+"F0.imprint","INTERSECT",VERTEX,{"derivedFrom":[subQ3,subQ0]});Q27=makeQuery(id+"F0.imprint","IMPRINT",FACE,{"disambiguationData":[TD([[makeQuery(id+"F0.imprint","IMPRINT",EDGE,{"disambiguationData":[TD([[subQ4,1.0]])],"derivedFrom":subQ3}),1.0]])]});}
            var Q28;
            {var subQ3=sQuery(id+"F0.wireOp",EDGE,"E27");var subQ5=sQuery(id+"F0.wireOp",EDGE,"E52");var subQ11=makeQuery(id+"F0.imprint","INTERSECT",VERTEX,{"derivedFrom":[subQ3,subQ5]});Q28=makeQuery(id+"F0.imprint","IMPRINT",FACE,{"disambiguationData":[TD([[makeQuery(id+"F0.imprint","IMPRINT",EDGE,{"disambiguationData":[TD([[subQ11,-1.0]])],"derivedFrom":subQ3}),1.0]])]});}
            var Q29;
            {var subQ2=sQuery(id+"F0.wireOp",EDGE,"E29");Q29=makeQuery(id+"F0.imprint","IMPRINT",FACE,{"disambiguationData":[TD([[makeQuery(id+"F0.imprint","IMPRINT",EDGE,{"derivedFrom":subQ2}),1.0]])]});}
            var Q30;
            {var subQ3=sQuery(id+"F0.wireOp",EDGE,"E28");Q30=makeQuery(id+"F0.imprint","IMPRINT",FACE,{"disambiguationData":[TD([[makeQuery(id+"F0.imprint","IMPRINT",EDGE,{"derivedFrom":subQ3}),-1.0]])]});}
            var Q31;
            {var subQ1=sQuery(id+"F0.wireOp",EDGE,"E5");var subQ5=sQuery(id+"F0.wireOp",EDGE,"E24");var subQ6=makeQuery(id+"F0.imprint","INTERSECT",VERTEX,{"derivedFrom":[subQ1,subQ5]});Q31=makeQuery(id+"F0.imprint","IMPRINT",FACE,{"disambiguationData":[TD([[makeQuery(id+"F0.imprint","IMPRINT",EDGE,{"disambiguationData":[TD([[subQ6,-1.0]])],"derivedFrom":subQ1}),-1.0]])]});}
            var Q32;
            {var subQ0=sQuery(id+"F0.wireOp",EDGE,"E25");var subQ1=sQuery(id+"F0.wireOp",EDGE,"E5");var subQ2=makeQuery(id+"F0.imprint","INTERSECT",VERTEX,{"derivedFrom":[subQ1,subQ0]});Q32=makeQuery(id+"F0.imprint","IMPRINT",FACE,{"disambiguationData":[TD([[makeQuery(id+"F0.imprint","IMPRINT",EDGE,{"disambiguationData":[TD([[subQ2,-1.0]])],"derivedFrom":subQ1}),-1.0]])]});}
            var Q33;
            {var subQ1=sQuery(id+"F0.wireOp",EDGE,"E5");var subQ5=sQuery(id+"F0.wireOp",EDGE,"E9");var subQ6=makeQuery(id+"F0.imprint","INTERSECT",VERTEX,{"derivedFrom":[subQ1,subQ5]});Q33=makeQuery(id+"F0.imprint","IMPRINT",FACE,{"disambiguationData":[TD([[makeQuery(id+"F0.imprint","IMPRINT",EDGE,{"disambiguationData":[TD([[subQ6,-1.0]])],"derivedFrom":subQ1}),-1.0]])]});}
            var Q34;
            {var subQ3=sQuery(id+"F0.wireOp",EDGE,"E34");Q34=makeQuery(id+"F0.imprint","IMPRINT",FACE,{"disambiguationData":[TD([[makeQuery(id+"F0.imprint","IMPRINT",EDGE,{"derivedFrom":subQ3}),1.0]])]});}
            var Q35;
            {var subQ1=sQuery(id+"F0.wireOp",EDGE,"E47");var subQ5=sQuery(id+"F0.wireOp",EDGE,"E51");var subQ6=makeQuery(id+"F0.imprint","INTERSECT",VERTEX,{"derivedFrom":[subQ1,subQ5]});Q35=makeQuery(id+"F0.imprint","IMPRINT",FACE,{"disambiguationData":[TD([[makeQuery(id+"F0.imprint","IMPRINT",EDGE,{"disambiguationData":[TD([[subQ6,-1.0]])],"derivedFrom":subQ1}),-1.0]])]});}
            var Q36;
            {var subQ5=sQuery(id+"F0.wireOp",EDGE,"E33");var subQ7=sQuery(id+"F0.wireOp",EDGE,"E52");var subQ9=makeQuery(id+"F0.imprint","INTERSECT",VERTEX,{"derivedFrom":[subQ5,subQ7]});Q36=makeQuery(id+"F0.imprint","IMPRINT",FACE,{"disambiguationData":[TD([[makeQuery(id+"F0.imprint","IMPRINT",EDGE,{"disambiguationData":[TD([[subQ9,-1.0]])],"derivedFrom":subQ5}),1.0]])]});}
            var Q37;
            {var subQ3=sQuery(id+"F0.wireOp",EDGE,"E31.right");var subQ5=sQuery(id+"F0.wireOp",EDGE,"E53");var subQ7=makeQuery(id+"F0.imprint","INTERSECT",VERTEX,{"derivedFrom":[subQ3,subQ5]});Q37=makeQuery(id+"F0.imprint","IMPRINT",FACE,{"disambiguationData":[TD([[makeQuery(id+"F0.imprint","IMPRINT",EDGE,{"disambiguationData":[TD([[subQ7,-1.0]])],"derivedFrom":subQ3}),-1.0]])]});}
            var Q38;
            {var subQ0=sQuery(id+"F0.wireOp",EDGE,"E58");Q38=makeQuery(id+"F0.imprint","IMPRINT",FACE,{"disambiguationData":[TD([[makeQuery(id+"F0.imprint","IMPRINT",EDGE,{"derivedFrom":subQ0}),-1.0]])]});}
            var Q39;
            {var subQ0=sQuery(id+"F0.wireOp",EDGE,"E54");var subQ3=sQuery(id+"F0.wireOp",EDGE,"E32");var subQ4=makeQuery(id+"F0.imprint","INTERSECT",VERTEX,{"derivedFrom":[subQ3,subQ0]});Q39=makeQuery(id+"F0.imprint","IMPRINT",FACE,{"disambiguationData":[TD([[makeQuery(id+"F0.imprint","IMPRINT",EDGE,{"disambiguationData":[TD([[subQ4,1.0]])],"derivedFrom":subQ3}),1.0]])]});}
            var Q40;
            {var subQ2=sQuery(id+"F0.wireOp",EDGE,"E49");Q40=makeQuery(id+"F0.imprint","IMPRINT",FACE,{"disambiguationData":[TD([[makeQuery(id+"F0.imprint","IMPRINT",EDGE,{"derivedFrom":subQ2}),1.0]])]});}
            var Q41;
            {var subQ3=sQuery(id+"F0.wireOp",EDGE,"E0.rect.left");var subQ5=sQuery(id+"F0.wireOp",EDGE,"E0.rect.bottom");var subQ7=makeQuery(id+"F0.imprint","INTERSECT",VERTEX,{"derivedFrom":[subQ5,subQ3]});Q41=makeQuery(id+"F0.imprint","IMPRINT",FACE,{"disambiguationData":[TD([[makeQuery(id+"F0.imprint","IMPRINT",EDGE,{"disambiguationData":[TD([[subQ7,-1.0]])],"derivedFrom":subQ3}),1.0]])]});}
            var Q42;
            {var subQ4=sQuery(id+"F0.wireOp",EDGE,"E48");Q42=makeQuery(id+"F0.imprint","IMPRINT",FACE,{"disambiguationData":[TD([[makeQuery(id+"F0.imprint","IMPRINT",EDGE,{"derivedFrom":subQ4}),-1.0]])]});}
            var Q43;
            {var subQ3=sQuery(id+"F0.wireOp",EDGE,"E0.rect.left");var subQ5=sQuery(id+"F0.wireOp",EDGE,"E53");var subQ7=makeQuery(id+"F0.imprint","INTERSECT",VERTEX,{"derivedFrom":[subQ3,subQ5]});Q43=makeQuery(id+"F0.imprint","IMPRINT",FACE,{"disambiguationData":[TD([[makeQuery(id+"F0.imprint","IMPRINT",EDGE,{"disambiguationData":[TD([[subQ7,1.0]])],"derivedFrom":subQ3}),1.0]])]});}
            var Q44;
            {var subQ3=sQuery(id+"F0.wireOp",EDGE,"E0.rect.left");var subQ5=sQuery(id+"F0.wireOp",EDGE,"E52");var subQ7=makeQuery(id+"F0.imprint","INTERSECT",VERTEX,{"derivedFrom":[subQ3,subQ5]});Q44=makeQuery(id+"F0.imprint","IMPRINT",FACE,{"disambiguationData":[TD([[makeQuery(id+"F0.imprint","IMPRINT",EDGE,{"disambiguationData":[TD([[subQ7,1.0]])],"derivedFrom":subQ3}),1.0]])]});}
            var Q45;
            {var subQ0=sQuery(id+"F0.wireOp",EDGE,"E51");var subQ3=sQuery(id+"F0.wireOp",EDGE,"E0.rect.left");var subQ4=makeQuery(id+"F0.imprint","INTERSECT",VERTEX,{"derivedFrom":[subQ3,subQ0]});Q45=makeQuery(id+"F0.imprint","IMPRINT",FACE,{"disambiguationData":[TD([[makeQuery(id+"F0.imprint","IMPRINT",EDGE,{"disambiguationData":[TD([[subQ4,1.0]])],"derivedFrom":subQ3}),1.0]])]});}
            var Q46;
            {var subQ1=sQuery(id+"F0.wireOp",EDGE,"E59");Q46=makeQuery(id+"F0.imprint","IMPRINT",FACE,{"disambiguationData":[TD([[makeQuery(id+"F0.imprint","IMPRINT",EDGE,{"derivedFrom":subQ1}),1.0]])]});}
            extrude(context, id + "F5", {"entities" : qUnion([Q0, Q1, Q2, Q3, Q4, Q5, Q6, Q7, Q8, Q9, Q10, Q11, Q12, Q13, Q14, Q15, Q16, Q17, Q18, Q19, Q20, Q21, Q22, Q23, Q24, Q25, Q26, Q27, Q28, Q29, Q30, Q31, Q32, Q33, Q34, Q35, Q36, Q37, Q38, Q39, Q40, Q41, Q42, Q43, Q44, Q45, Q46]), "depth" : 19.05 * mm});
        }
        {
            var Q0;
            Q0=makeQuery(id+"F5.opExtrude","SWEPT_BODY",BODY,{"disambiguationData":[OSD([sQuery(id+"F0.wireOp",EDGE,"E0.rect.bottom"),sQuery(id+"F0.wireOp",EDGE,"E0.rect.top"),sQuery(id+"F0.wireOp",EDGE,"E0.rect.left"),sQuery(id+"F0.wireOp",EDGE,"E0.rect.right"),sQuery(id+"F0.wireOp",EDGE,"E1"),sQuery(id+"F0.wireOp",EDGE,"E2"),sQuery(id+"F0.wireOp",EDGE,"E3"),sQuery(id+"F0.wireOp",EDGE,"E6"),sQuery(id+"F0.wireOp",EDGE,"E7"),sQuery(id+"F0.wireOp",EDGE,"E8"),sQuery(id+"F0.wireOp",EDGE,"E11"),sQuery(id+"F0.wireOp",EDGE,"E19"),sQuery(id+"F0.wireOp",EDGE,"E20"),sQuery(id+"F0.wireOp",EDGE,"E22"),sQuery(id+"F0.wireOp",EDGE,"E23"),sQuery(id+"F0.wireOp",EDGE,"E26"),sQuery(id+"F0.wireOp",EDGE,"E27"),sQuery(id+"F0.wireOp",EDGE,"E28"),sQuery(id+"F0.wireOp",EDGE,"E29"),sQuery(id+"F0.wireOp",EDGE,"E30.left"),sQuery(id+"F0.wireOp",EDGE,"E30.right"),sQuery(id+"F0.wireOp",EDGE,"E31.left"),sQuery(id+"F0.wireOp",EDGE,"E31.right"),sQuery(id+"F0.wireOp",EDGE,"E32"),sQuery(id+"F0.wireOp",EDGE,"E33"),sQuery(id+"F0.wireOp",EDGE,"E34"),sQuery(id+"F0.wireOp",EDGE,"E35"),sQuery(id+"F0.wireOp",EDGE,"E42"),sQuery(id+"F0.wireOp",EDGE,"E43"),sQuery(id+"F0.wireOp",EDGE,"E44"),sQuery(id+"F0.wireOp",EDGE,"E46"),sQuery(id+"F0.wireOp",EDGE,"E47"),sQuery(id+"F0.wireOp",EDGE,"E48"),sQuery(id+"F0.wireOp",EDGE,"E52"),sQuery(id+"F0.wireOp",EDGE,"E53"),sQuery(id+"F0.wireOp",EDGE,"E54"),sQuery(id+"F0.wireOp",EDGE,"E55"),sQuery(id+"F0.wireOp",EDGE,"E56"),sQuery(id+"F0.wireOp",EDGE,"E57"),sQuery(id+"F0.wireOp",EDGE,"E58")])]});
            transform(context, id + "F6", {"entities" : qUnion([Q0]), "transformType" : TransformType.TRANSLATION_3D, "dx" : 0 * mm, "dy" : 0 * mm, "dz" : -571.5 * mm, "makeCopy" : false});
        }
        {
            var Q0;
            {var subQ1=sQuery(id+"F0.wireOp",EDGE,"E4");var subQ5=sQuery(id+"F0.wireOp",EDGE,"E9");var subQ7=makeQuery(id+"F0.imprint","INTERSECT",VERTEX,{"derivedFrom":[subQ1,subQ5]});Q0=makeQuery(id+"F0.imprint","IMPRINT",FACE,{"disambiguationData":[TD([[makeQuery(id+"F0.imprint","IMPRINT",EDGE,{"disambiguationData":[TD([[subQ7,-1.0]])],"derivedFrom":subQ1}),1.0]])]});}
            var Q1;
            {var subQ3=sQuery(id+"F0.wireOp",EDGE,"E4");var subQ5=sQuery(id+"F0.wireOp",EDGE,"E9");var subQ7=makeQuery(id+"F0.imprint","INTERSECT",VERTEX,{"derivedFrom":[subQ3,subQ5]});Q1=makeQuery(id+"F0.imprint","IMPRINT",FACE,{"disambiguationData":[TD([[makeQuery(id+"F0.imprint","IMPRINT",EDGE,{"disambiguationData":[TD([[subQ7,-1.0]])],"derivedFrom":subQ3}),-1.0]])]});}
            var Q2;
            {var subQ1=sQuery(id+"F0.wireOp",EDGE,"E5");var subQ5=sQuery(id+"F0.wireOp",EDGE,"E9");var subQ6=makeQuery(id+"F0.imprint","INTERSECT",VERTEX,{"derivedFrom":[subQ1,subQ5]});Q2=makeQuery(id+"F0.imprint","IMPRINT",FACE,{"disambiguationData":[TD([[makeQuery(id+"F0.imprint","IMPRINT",EDGE,{"disambiguationData":[TD([[subQ6,-1.0]])],"derivedFrom":subQ1}),-1.0]])]});}
            var Q3;
            {var subQ0=sQuery(id+"F0.wireOp",EDGE,"E25");var subQ1=sQuery(id+"F0.wireOp",EDGE,"E5");var subQ2=makeQuery(id+"F0.imprint","INTERSECT",VERTEX,{"derivedFrom":[subQ1,subQ0]});Q3=makeQuery(id+"F0.imprint","IMPRINT",FACE,{"disambiguationData":[TD([[makeQuery(id+"F0.imprint","IMPRINT",EDGE,{"disambiguationData":[TD([[subQ2,-1.0]])],"derivedFrom":subQ1}),-1.0]])]});}
            var Q4;
            {var subQ0=sQuery(id+"F0.wireOp",EDGE,"E25");var subQ3=sQuery(id+"F0.wireOp",EDGE,"E4");var subQ4=makeQuery(id+"F0.imprint","INTERSECT",VERTEX,{"derivedFrom":[subQ3,subQ0]});Q4=makeQuery(id+"F0.imprint","IMPRINT",FACE,{"disambiguationData":[TD([[makeQuery(id+"F0.imprint","IMPRINT",EDGE,{"disambiguationData":[TD([[subQ4,-1.0]])],"derivedFrom":subQ3}),-1.0]])]});}
            var Q5;
            {var subQ0=sQuery(id+"F0.wireOp",EDGE,"E25");var subQ1=sQuery(id+"F0.wireOp",EDGE,"E4");var subQ2=makeQuery(id+"F0.imprint","INTERSECT",VERTEX,{"derivedFrom":[subQ1,subQ0]});Q5=makeQuery(id+"F0.imprint","IMPRINT",FACE,{"disambiguationData":[TD([[makeQuery(id+"F0.imprint","IMPRINT",EDGE,{"disambiguationData":[TD([[subQ2,-1.0]])],"derivedFrom":subQ1}),1.0]])]});}
            extrude(context, id + "F7", {"entities" : qUnion([Q0, Q1, Q2, Q3, Q4, Q5]), "oppositeDirection" : true, "depth" : 88.9 * mm});
        }
        {
            var Q0;
            Q0=makeQuery(id+"F4.opExtrude","SWEPT_FACE",FACE,{"disambiguationData":[OSD([sQuery(id+"F0.wireOp",EDGE,"E27")])]});
            var sketch = newSketch(context, id + "F8", { "sketchPlane" : qUnion([Q0])});
            skLineSegment(sketch, "E83", {"start": v(-152.4, 0) * mm, "end": v(-63.5, 0) * mm, "construction": true});
            skLineSegment(sketch, "E84", {"start": v(-63.5, 0) * mm, "end": v(25.4, 0) * mm, "construction": true});
            skLineSegment(sketch, "E85", {"start": v(-63.5, 0) * mm, "end": v(-63.5, -609.6) * mm, "construction": true});
            skLineSegment(sketch, "E86", {"start": v(25.4, 0) * mm, "end": v(25.4, -88.9) * mm});
            skLineSegment(sketch, "E87", {"start": v(25.4, -88.9) * mm, "end": v(292.1, -88.9) * mm});
            skLineSegment(sketch, "E88", {"start": v(292.1, -88.9) * mm, "end": v(292.1, 0) * mm});
            skLineSegment(sketch, "E89", {"start": v(292.1, 0) * mm, "end": v(25.4, 0) * mm});
            skLineSegment(sketch, "E90", {"start": v(25.4, -44.45) * mm, "end": v(114.3, -44.45) * mm, "construction": true});
            skLineSegment(sketch, "E91", {"start": v(114.3, -44.45) * mm, "end": v(203.2, -44.45) * mm, "construction": true});
            skLineSegment(sketch, "E92", {"start": v(203.2, -44.45) * mm, "end": v(292.1, -44.45) * mm, "construction": true});
            skCircle(sketch, "E93", {"center": v(158.75, -44.45) * mm, "radius": 15.88 * mm});
            skCircle(sketch, "E94", {"center": v(69.85, -44.45) * mm, "radius": 15.88 * mm});
            skPoint(sketch, "E95", {"position": v(-63.5, -552.45) * mm});
            skLineSegment(sketch, "E96", {"start": v(-107.95, 0) * mm, "end": v(-107.95, -552.45) * mm, "construction": true});
            skLineSegment(sketch, "E97", {"start": v(-19.05, 0) * mm, "end": v(-19.05, -552.45) * mm, "construction": true});
            skCircle(sketch, "E98", {"center": v(-107.95, -276.23) * mm, "radius": 15.88 * mm});
            skCircle(sketch, "E99", {"center": v(-19.05, -276.23) * mm, "radius": 15.88 * mm});
            skCircle(sketch, "E100", {"center": v(-19.05, -276.23) * mm, "radius": 292.12 * mm, "construction": true});
            skCircle(sketch, "E101", {"center": v(-107.95, -276.23) * mm, "radius": 292.12 * mm, "construction": true});
            skPoint(sketch, "E102", {"position": v(-266.7, -31.75) * mm});
            skCircle(sketch, "E103", {"center": v(-266.7, -31.75) * mm, "radius": 15.88 * mm});
            skCircle(sketch, "E104", {"center": v(-19.05, -276.23) * mm, "radius": 348 * mm, "construction": true});
            skLineSegment(sketch, "E105.rect.bottom", {"start": v(298.45, -250.83) * mm, "end": v(-336.55, -250.82) * mm});
            skLineSegment(sketch, "E105.rect.top", {"start": v(298.45, -301.63) * mm, "end": v(-336.55, -301.62) * mm});
            skLineSegment(sketch, "E105.rect.left", {"start": v(298.45, -250.83) * mm, "end": v(298.45, -301.63) * mm});
            skLineSegment(sketch, "E105.rect.right", {"start": v(-336.55, -250.82) * mm, "end": v(-336.55, -301.62) * mm});
            skCircle(sketch, "E106", {"center": v(184.17, -276.23) * mm, "radius": 15.88 * mm});
            skCircle(sketch, "E107", {"center": v(-367.04, -276.23) * mm, "radius": 15.88 * mm});
            skLineSegment(sketch, "E108", {"start": v(-336.55, -250.82) * mm, "end": v(-398.96, -250.82) * mm});
            skLineSegment(sketch, "E109", {"start": v(-398.96, -250.82) * mm, "end": v(-398.96, -301.63) * mm});
            skLineSegment(sketch, "E110", {"start": v(-398.96, -301.63) * mm, "end": v(-336.55, -301.63) * mm});
            skLineSegment(sketch, "E111", {"start": v(-152.4, -250.82) * mm, "end": v(-152.4, -301.63) * mm});
            skLineSegment(sketch, "E112", {"start": v(203.2, -250.82) * mm, "end": v(203.2, -301.63) * mm});
            skCircle(sketch, "E113", {"center": v(273.07, -276.23) * mm, "radius": 15.88 * mm});
            skSolve(sketch);
        }
        {
            var Q0;
            Q0=makeQuery(id+"F8.imprint","IMPRINT",FACE,{"disambiguationData":[TD([[makeQuery(id+"F8.imprint","IMPRINT",EDGE,{"derivedFrom":sQuery(id+"F8.wireOp",EDGE,"E98")}),1.0]])]});
            var Q1;
            Q1=makeQuery(id+"F8.imprint","IMPRINT",FACE,{"disambiguationData":[TD([[makeQuery(id+"F8.imprint","IMPRINT",EDGE,{"derivedFrom":sQuery(id+"F8.wireOp",EDGE,"E99")}),1.0]])]});
            var Q2;
            Q2=makeQuery(id+"F8.imprint","IMPRINT",FACE,{"disambiguationData":[TD([[makeQuery(id+"F8.imprint","IMPRINT",EDGE,{"derivedFrom":sQuery(id+"F8.wireOp",EDGE,"E94")}),1.0]])]});
            var Q3;
            Q3=makeQuery(id+"F8.imprint","IMPRINT",FACE,{"disambiguationData":[TD([[makeQuery(id+"F8.imprint","IMPRINT",EDGE,{"derivedFrom":sQuery(id+"F8.wireOp",EDGE,"E93")}),1.0]])]});
            extrude(context, id + "F9", {"entities" : qUnion([Q0, Q1, Q2, Q3]), "operationType" : NewBodyOperationType.REMOVE, "oppositeDirection" : true, "depth" : 76.2 * mm});
        }
        {
            var Q0;
            Q0=makeQuery(id+"F8.imprint","IMPRINT",FACE,{"disambiguationData":[TD([[makeQuery(id+"F8.imprint","IMPRINT",EDGE,{"derivedFrom":sQuery(id+"F8.wireOp",EDGE,"E105.rect.right")}),-1.0]])]});
            var Q1;
            {var subQ1=sQuery(id+"F8.wireOp",EDGE,"E105.rect.right");Q1=makeQuery(id+"F8.imprint","IMPRINT",FACE,{"disambiguationData":[TD([[makeQuery(id+"F8.imprint","IMPRINT",EDGE,{"derivedFrom":subQ1}),1.0]])]});}
            var Q2;
            Q2=makeQuery(id+"F8.imprint","IMPRINT",FACE,{"disambiguationData":[TD([[makeQuery(id+"F8.imprint","IMPRINT",EDGE,{"derivedFrom":sQuery(id+"F8.wireOp",EDGE,"E98")}),-1.0]])]});
            var Q3;
            Q3=makeQuery(id+"F8.imprint","IMPRINT",FACE,{"disambiguationData":[TD([[makeQuery(id+"F8.imprint","IMPRINT",EDGE,{"derivedFrom":sQuery(id+"F8.wireOp",EDGE,"E98")}),1.0]])]});
            var Q4;
            Q4=makeQuery(id+"F8.imprint","IMPRINT",FACE,{"disambiguationData":[TD([[makeQuery(id+"F8.imprint","IMPRINT",EDGE,{"derivedFrom":sQuery(id+"F8.wireOp",EDGE,"E106")}),-1.0]])]});
            var Q5;
            Q5=makeQuery(id+"F8.imprint","IMPRINT",FACE,{"disambiguationData":[TD([[makeQuery(id+"F8.imprint","IMPRINT",EDGE,{"derivedFrom":sQuery(id+"F8.wireOp",EDGE,"E106")}),1.0]])]});
            var Q6;
            {var subQ1=sQuery(id+"F8.wireOp",EDGE,"E105.rect.left");Q6=makeQuery(id+"F8.imprint","IMPRINT",FACE,{"disambiguationData":[TD([[makeQuery(id+"F8.imprint","IMPRINT",EDGE,{"derivedFrom":subQ1}),-1.0]])]});}
            extrude(context, id + "F10", {"entities" : qUnion([Q0, Q1, Q2, Q3, Q4, Q5, Q6]), "depth" : 25.4 * mm});
        }
        {
            var Q0;
            Q0=makeQuery(id+"F8.imprint","IMPRINT",FACE,{"disambiguationData":[TD([[makeQuery(id+"F8.imprint","IMPRINT",EDGE,{"derivedFrom":sQuery(id+"F8.wireOp",EDGE,"E103")}),1.0]])]});
            extrude(context, id + "F11", {"entities" : qUnion([Q0]), "oppositeDirection" : true, "depth" : 127 * mm});
        }
        {
            var Q0;
            Q0=makeQuery(id+"F8.imprint","IMPRINT",FACE,{"disambiguationData":[TD([[makeQuery(id+"F8.imprint","IMPRINT",EDGE,{"derivedFrom":sQuery(id+"F8.wireOp",EDGE,"E106")}),-1.0]])]});
            var Q1;
            Q1=makeQuery(id+"F8.imprint","IMPRINT",FACE,{"disambiguationData":[TD([[makeQuery(id+"F8.imprint","IMPRINT",EDGE,{"derivedFrom":sQuery(id+"F8.wireOp",EDGE,"E98")}),-1.0]])]});
            var Q2;
            Q2=makeQuery(id+"F8.imprint","IMPRINT",FACE,{"disambiguationData":[TD([[makeQuery(id+"F8.imprint","IMPRINT",EDGE,{"derivedFrom":sQuery(id+"F8.wireOp",EDGE,"E99")}),1.0]])]});
            extrude(context, id + "F12", {"entities" : qUnion([Q0, Q1, Q2]), "oppositeDirection" : true, "depth" : 25.4 * mm});
        }
        {
            var Q0;
            Q0=makeQuery(id+"F12.opExtrude","SWEPT_BODY",BODY,{"disambiguationData":[OSD([sQuery(id+"F8.wireOp",EDGE,"E98"),sQuery(id+"F8.wireOp",EDGE,"E105.rect.bottom"),sQuery(id+"F8.wireOp",EDGE,"E105.rect.top"),sQuery(id+"F8.wireOp",EDGE,"E106"),sQuery(id+"F8.wireOp",EDGE,"E111"),sQuery(id+"F8.wireOp",EDGE,"E112")])]});
            transform(context, id + "F13", {"entities" : qUnion([Q0]), "transformType" : TransformType.TRANSLATION_3D, "dx" : -38.1 * mm, "dy" : 0 * mm, "dz" : 0 * mm, "makeCopy" : false});
        }
        {
            var Q0;
            {var subQ1=sQuery(id+"F0.wireOp",EDGE,"E4");var subQ5=sQuery(id+"F0.wireOp",EDGE,"E24");var subQ6=makeQuery(id+"F0.imprint","INTERSECT",VERTEX,{"derivedFrom":[subQ1,subQ5]});Q0=makeQuery(id+"F0.imprint","IMPRINT",FACE,{"disambiguationData":[TD([[makeQuery(id+"F0.imprint","IMPRINT",EDGE,{"disambiguationData":[TD([[subQ6,-1.0]])],"derivedFrom":subQ1}),1.0]])]});}
            var Q1;
            {var subQ0=sQuery(id+"F0.wireOp",EDGE,"E25");var subQ1=sQuery(id+"F0.wireOp",EDGE,"E4");var subQ2=makeQuery(id+"F0.imprint","INTERSECT",VERTEX,{"derivedFrom":[subQ1,subQ0]});Q1=makeQuery(id+"F0.imprint","IMPRINT",FACE,{"disambiguationData":[TD([[makeQuery(id+"F0.imprint","IMPRINT",EDGE,{"disambiguationData":[TD([[subQ2,-1.0]])],"derivedFrom":subQ1}),1.0]])]});}
            var Q2;
            {var subQ0=sQuery(id+"F0.wireOp",EDGE,"E22");Q2=makeQuery(id+"F0.imprint","IMPRINT",FACE,{"disambiguationData":[TD([[makeQuery(id+"F0.imprint","IMPRINT",EDGE,{"derivedFrom":subQ0}),1.0]])]});}
            var Q3;
            {var subQ0=sQuery(id+"F0.wireOp",EDGE,"E11");var subQ4=sQuery(id+"F0.wireOp",EDGE,"E4");var subQ5=makeQuery(id+"F0.imprint","INTERSECT",VERTEX,{"derivedFrom":[subQ4,subQ0]});Q3=makeQuery(id+"F0.imprint","IMPRINT",FACE,{"disambiguationData":[TD([[makeQuery(id+"F0.imprint","IMPRINT",EDGE,{"disambiguationData":[TD([[subQ5,1.0]])],"derivedFrom":subQ4}),-1.0]])]});}
            var Q4;
            {var subQ5=sQuery(id+"F0.wireOp",EDGE,"E8");Q4=makeQuery(id+"F0.imprint","IMPRINT",FACE,{"disambiguationData":[TD([[makeQuery(id+"F0.imprint","IMPRINT",EDGE,{"derivedFrom":subQ5}),-1.0]])]});}
            var Q5;
            {var subQ0=sQuery(id+"F0.wireOp",EDGE,"E25");var subQ1=sQuery(id+"F0.wireOp",EDGE,"E5");var subQ2=makeQuery(id+"F0.imprint","INTERSECT",VERTEX,{"derivedFrom":[subQ1,subQ0]});Q5=makeQuery(id+"F0.imprint","IMPRINT",FACE,{"disambiguationData":[TD([[makeQuery(id+"F0.imprint","IMPRINT",EDGE,{"disambiguationData":[TD([[subQ2,-1.0]])],"derivedFrom":subQ1}),-1.0]])]});}
            var Q6;
            {var subQ0=sQuery(id+"F0.wireOp",EDGE,"E25");var subQ3=sQuery(id+"F0.wireOp",EDGE,"E4");var subQ4=makeQuery(id+"F0.imprint","INTERSECT",VERTEX,{"derivedFrom":[subQ3,subQ0]});Q6=makeQuery(id+"F0.imprint","IMPRINT",FACE,{"disambiguationData":[TD([[makeQuery(id+"F0.imprint","IMPRINT",EDGE,{"disambiguationData":[TD([[subQ4,-1.0]])],"derivedFrom":subQ3}),-1.0]])]});}
            var Q7;
            {var subQ3=sQuery(id+"F0.wireOp",EDGE,"E4");var subQ5=sQuery(id+"F0.wireOp",EDGE,"E24");var subQ7=makeQuery(id+"F0.imprint","INTERSECT",VERTEX,{"derivedFrom":[subQ3,subQ5]});Q7=makeQuery(id+"F0.imprint","IMPRINT",FACE,{"disambiguationData":[TD([[makeQuery(id+"F0.imprint","IMPRINT",EDGE,{"disambiguationData":[TD([[subQ7,-1.0]])],"derivedFrom":subQ3}),-1.0]])]});}
            var Q8;
            {var subQ1=sQuery(id+"F0.wireOp",EDGE,"E5");var subQ5=sQuery(id+"F0.wireOp",EDGE,"E24");var subQ6=makeQuery(id+"F0.imprint","INTERSECT",VERTEX,{"derivedFrom":[subQ1,subQ5]});Q8=makeQuery(id+"F0.imprint","IMPRINT",FACE,{"disambiguationData":[TD([[makeQuery(id+"F0.imprint","IMPRINT",EDGE,{"disambiguationData":[TD([[subQ6,-1.0]])],"derivedFrom":subQ1}),-1.0]])]});}
            var Q9;
            {var subQ1=sQuery(id+"F0.wireOp",EDGE,"E5");var subQ5=sQuery(id+"F0.wireOp",EDGE,"E9");var subQ6=makeQuery(id+"F0.imprint","INTERSECT",VERTEX,{"derivedFrom":[subQ1,subQ5]});Q9=makeQuery(id+"F0.imprint","IMPRINT",FACE,{"disambiguationData":[TD([[makeQuery(id+"F0.imprint","IMPRINT",EDGE,{"disambiguationData":[TD([[subQ6,-1.0]])],"derivedFrom":subQ1}),-1.0]])]});}
            var Q10;
            {var subQ3=sQuery(id+"F0.wireOp",EDGE,"E4");var subQ5=sQuery(id+"F0.wireOp",EDGE,"E9");var subQ7=makeQuery(id+"F0.imprint","INTERSECT",VERTEX,{"derivedFrom":[subQ3,subQ5]});Q10=makeQuery(id+"F0.imprint","IMPRINT",FACE,{"disambiguationData":[TD([[makeQuery(id+"F0.imprint","IMPRINT",EDGE,{"disambiguationData":[TD([[subQ7,-1.0]])],"derivedFrom":subQ3}),-1.0]])]});}
            var Q11;
            {var subQ1=sQuery(id+"F0.wireOp",EDGE,"E4");var subQ5=sQuery(id+"F0.wireOp",EDGE,"E9");var subQ7=makeQuery(id+"F0.imprint","INTERSECT",VERTEX,{"derivedFrom":[subQ1,subQ5]});Q11=makeQuery(id+"F0.imprint","IMPRINT",FACE,{"disambiguationData":[TD([[makeQuery(id+"F0.imprint","IMPRINT",EDGE,{"disambiguationData":[TD([[subQ7,-1.0]])],"derivedFrom":subQ1}),1.0]])]});}
            var Q12;
            {var subQ0=sQuery(id+"F0.wireOp",EDGE,"E20");Q12=makeQuery(id+"F0.imprint","IMPRINT",FACE,{"disambiguationData":[TD([[makeQuery(id+"F0.imprint","IMPRINT",EDGE,{"derivedFrom":subQ0}),1.0]])]});}
            var Q13;
            {var subQ0=sQuery(id+"F0.wireOp",EDGE,"E9");var subQ3=sQuery(id+"F0.wireOp",EDGE,"E4");var subQ4=makeQuery(id+"F0.imprint","INTERSECT",VERTEX,{"derivedFrom":[subQ3,subQ0]});Q13=makeQuery(id+"F0.imprint","IMPRINT",FACE,{"disambiguationData":[TD([[makeQuery(id+"F0.imprint","IMPRINT",EDGE,{"disambiguationData":[TD([[subQ4,-1.0]])],"derivedFrom":subQ0}),-1.0]])]});}
            var Q14;
            {var subQ5=sQuery(id+"F0.wireOp",EDGE,"E7");Q14=makeQuery(id+"F0.imprint","IMPRINT",FACE,{"disambiguationData":[TD([[makeQuery(id+"F0.imprint","IMPRINT",EDGE,{"derivedFrom":subQ5}),1.0]])]});}
            extrude(context, id + "F14", {"entities" : qUnion([Q0, Q1, Q2, Q3, Q4, Q5, Q6, Q7, Q8, Q9, Q10, Q11, Q12, Q13, Q14]), "operationType" : NewBodyOperationType.ADD, "depth" : 38.1 * mm});
        }
    });
